# Revit family: Zumtobel PANOS EVO R150
name_source: partatom
category: Lighting Fixtures
revit_build: Autodesk Revit 2016 (Build: 20150220_1215(x64)
units: mm (PartAtom-declared; Revit-internal decimal feet)

## family parameters
Cut with Voids When Loaded = No
Host = Face
Light Source = Yes
OmniClass Number = 23.80.70.11
OmniClass Title = Luminaries for Internal Lighting
Part Type = Normal
Room Calculation Point = No
Round Connector Dimension = Use Diameter
Shared = No

## types (3) — shared parameters
Assembly Code = D5020200
Body = Zumtobel_Metal_White
Color Filter = 16777215
Description = LED ceiling-recessed luminaire
Dimming Lamp Color Temperature Shift = <None>
Emit Shape Visible in Rendering = Yes
Emit from Circle Diameter = 168 mm  [stored 0.551181 ft]
Lamp = LED
Length = 168 mm  [stored 0.551181 ft]
Manufacturer = Zumtobel Lighting
Reflector = Zumtobel_Metal_White_Self_Illumination
Tilt Angle = -90.00°
URL = http://www.zumtobel.com
Voltage = 230 V
Width = 168 mm  [stored 0.551181 ft]
zero-valued in all types: Default Elevation

## per-type parameters (varying)
| type | Apparent Load | Body Height | Cooling Unit Height | Height | Model | Opening Case Height | Photometric Web File |
| PANOS EVO R150H 10W LED840 LDO AL WH | 16 VA | 30 mm  [stored 0.0984252 ft] | 50 mm  [stored 0.164042 ft] | 103 mm  [stored 0.337927 ft] | 60816039 | 13 mm | 60816039_(STD_LEO).IES |
| PANOS EVO R150H 16W LED840 LDO AL WH | 16 VA | 30 mm  [stored 0.0984252 ft] | 50 mm  [stored 0.164042 ft] | 103 mm  [stored 0.337927 ft] | 60816039 | 13 mm | 60816039_(STD_LEO).IES |
| P-INF R150L | 14 VA | 17 mm | 28 mm  [stored 0.0918635 ft] | 65 mm  [stored 0.213255 ft] | 60818490 | 35 mm  [stored 0.114829 ft] | 60818490_(STD_LEO).IES |

note: [stored X ft] marks values corroborated as IEEE doubles in the binary element streams (Revit-internal decimal feet)

## geometry (parser evidence)
native form markers: Sweep x6
no freeform markers — native parametric forms only
